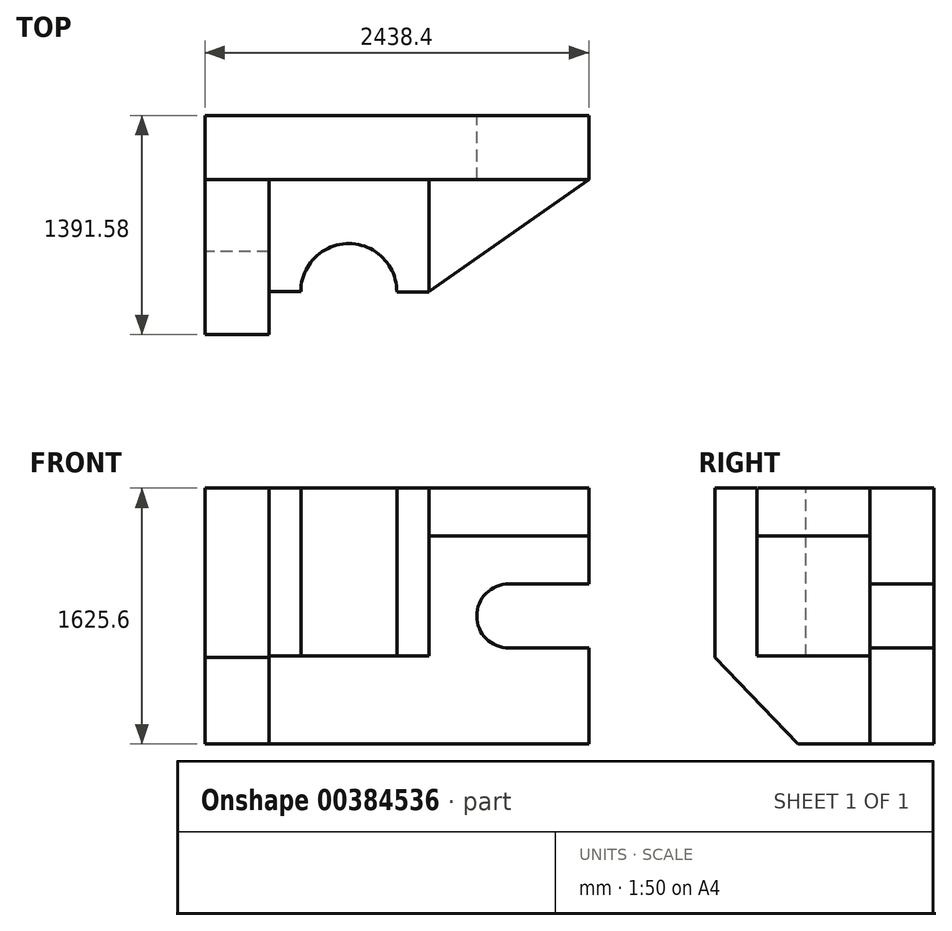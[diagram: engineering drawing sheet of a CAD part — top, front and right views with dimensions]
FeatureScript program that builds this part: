
annotation { "Feature Type Name" : "Feature", "Feature Type Description" : "" }
export const myFeature = defineFeature(function(context is Context, id is Id, definition is map)
    precondition{}
    {
        {
            var Q0;
            Q0=qCreatedBy(makeId("Front.planeOp"),FACE);
            var sketch = newSketch(context, id + "F0", { "sketchPlane" : qUnion([Q0])});
            skLineSegment(sketch, "E0", {"start": v(-484.81, -337.27) * mm, "end": v(1953.59, -337.27) * mm});
            skLineSegment(sketch, "E1", {"start": v(1953.59, -337.27) * mm, "end": v(1953.59, 272.33) * mm});
            skLineSegment(sketch, "E2", {"start": v(1953.59, 1288.33) * mm, "end": v(-484.81, 1288.33) * mm});
            skLineSegment(sketch, "E3", {"start": v(-484.81, 1288.33) * mm, "end": v(-484.81, -337.27) * mm});
            skArc(sketch, "E4", {"start": v(1445.59, 678.73) * mm, "mid": v(1242.39, 475.53) * mm, "end": v(1445.59, 272.33) * mm});
            skLineSegment(sketch, "E5", {"start": v(1445.59, 678.73) * mm, "end": v(1953.59, 678.73) * mm});
            skLineSegment(sketch, "E6", {"start": v(1445.59, 272.33) * mm, "end": v(1953.59, 272.33) * mm});
            skLineSegment(sketch, "E7.trimOffspring", {"start": v(1953.59, 678.73) * mm, "end": v(1953.59, 1288.33) * mm});
            skSolve(sketch);
        }
        {
            var Q0;
            Q0=makeQuery(id+"F0.imprint","IMPRINT",FACE,{"disambiguationData":[TD([[makeQuery(id+"F0.imprint","IMPRINT",EDGE,{"derivedFrom":sQuery(id+"F0.wireOp",EDGE,"E0")}),1.0]])]});
            extrude(context, id + "F1", {"entities" : qUnion([Q0]), "depth" : 406.4 * mm});
        }
        {
            var Q0;
            Q0=makeQuery(id+"F1.opExtrude","SWEPT_FACE",FACE,{"disambiguationData":[OSD([sQuery(id+"F0.wireOp",EDGE,"E2")])]});
            var sketch = newSketch(context, id + "F2", { "sketchPlane" : qUnion([Q0])});
            skLineSegment(sketch, "E8", {"start": v(937.59, -406.4) * mm, "end": v(937.59, -1117.6) * mm});
            skLineSegment(sketch, "E9", {"start": v(937.59, -1117.6) * mm, "end": v(1953.59, -406.4) * mm});
            skSolve(sketch);
        }
        {
            var Q0;
            {var subQ0=sQuery(id+"F2.wireOp",EDGE,"E8");Q0=makeQuery(id+"F2.imprint","IMPRINT",FACE,{"disambiguationData":[TD([[makeQuery(id+"F2.imprint","IMPRINT",EDGE,{"derivedFrom":subQ0}),1.0]])]});}
            extrude(context, id + "F3", {"entities" : qUnion([Q0]), "depth" : -304.8 * mm});
        }
        {
            var Q0;
            Q0=makeQuery(id+"F1.opExtrude","SWEPT_FACE",FACE,{"disambiguationData":[OSD([sQuery(id+"F0.wireOp",EDGE,"E2")])]});
            var sketch = newSketch(context, id + "F4", { "sketchPlane" : qUnion([Q0])});
            skLineSegment(sketch, "E10", {"start": v(-78.41, -406.4) * mm, "end": v(-78.41, -1003.77) * mm});
            skLineSegment(sketch, "E11", {"start": v(-78.41, -1003.77) * mm, "end": v(-78.41, -1117.6) * mm});
            skArc(sketch, "E12", {"start": v(734.44, -1121.89) * mm, "mid": v(431.27, -813.83) * mm, "end": v(124.84, -1118.64) * mm});
            skLineSegment(sketch, "E13", {"start": v(-78.41, -1117.6) * mm, "end": v(124.84, -1118.64) * mm});
            skLineSegment(sketch, "E14", {"start": v(734.44, -1121.89) * mm, "end": v(937.64, -1121.89) * mm});
            skLineSegment(sketch, "E15", {"start": v(734.44, -1121.89) * mm, "end": v(734.44, -1115.38) * mm});
            skLineSegment(sketch, "E16", {"start": v(937.64, -1121.89) * mm, "end": v(937.64, -406.4) * mm});
            skPoint(sketch, "E17.orphan", {"position": v(734.44, -406.4) * mm});
            skSolve(sketch);
        }
        {
            var Q0;
            {var subQ5=sQuery(id+"F4.wireOp",EDGE,"E10");Q0=makeQuery(id+"F4.imprint","IMPRINT",FACE,{"disambiguationData":[TD([[makeQuery(id+"F4.imprint","IMPRINT",EDGE,{"derivedFrom":subQ5}),1.0]])]});}
            extrude(context, id + "F5", {"entities" : qUnion([Q0]), "depth" : -1066.8 * mm});
        }
        {
            var Q0;
            Q0=makeQuery(id+"F1.opExtrude","SWEPT_FACE",FACE,{"disambiguationData":[OSD([sQuery(id+"F0.wireOp",EDGE,"E3")])]});
            var sketch = newSketch(context, id + "F6", { "sketchPlane" : qUnion([Q0])});
            skLineSegment(sketch, "E18", {"start": v(406.4, -337.27) * mm, "end": v(863.6, -337.27) * mm});
            skLineSegment(sketch, "E19", {"start": v(406.4, 1288.33) * mm, "end": v(1391.58, 1288.33) * mm});
            skLineSegment(sketch, "E20", {"start": v(1391.58, 1288.33) * mm, "end": v(1391.58, 212.17) * mm});
            skLineSegment(sketch, "E21", {"start": v(863.6, -337.27) * mm, "end": v(1391.58, 212.17) * mm});
            skSolve(sketch);
        }
        {
            var Q0;
            Q0=makeQuery(id+"F6.imprint","IMPRINT",FACE,{"disambiguationData":[TD([[makeQuery(id+"F6.imprint","IMPRINT",EDGE,{"derivedFrom":sQuery(id+"F6.wireOp",EDGE,"E18")}),1.0]])]});
            extrude(context, id + "F7", {"entities" : qUnion([Q0]), "depth" : -406.4 * mm});
        }
    });
